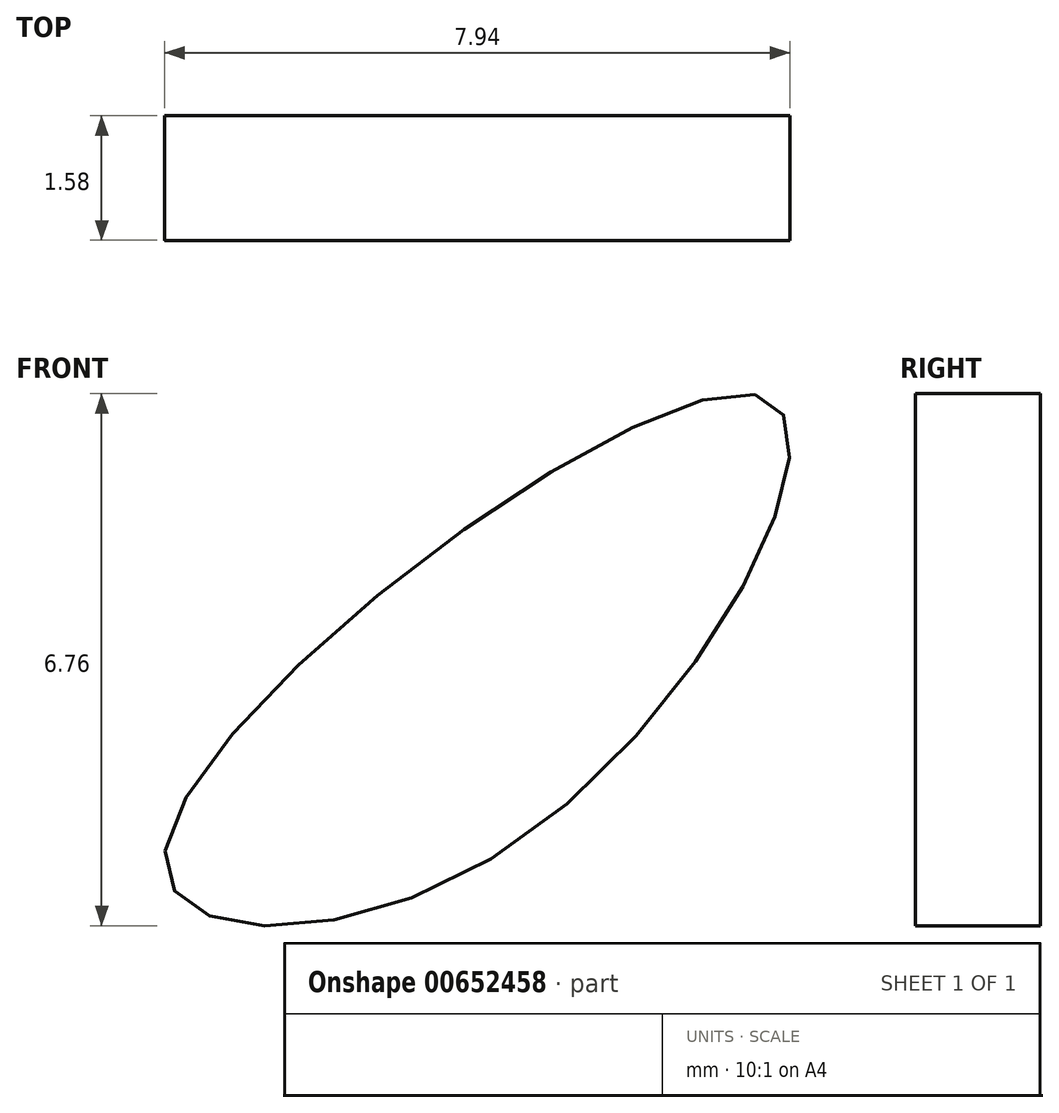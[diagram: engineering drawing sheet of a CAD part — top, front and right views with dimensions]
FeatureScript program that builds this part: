
annotation { "Feature Type Name" : "Feature", "Feature Type Description" : "" }
export const myFeature = defineFeature(function(context is Context, id is Id, definition is map)
    precondition{}
    {
        {
            var Q0;
            Q0=qCreatedBy(makeId("Front.planeOp"),FACE);
            var sketch = newSketch(context, id + "F0", { "sketchPlane" : qUnion([Q0])});
            skFitSpline(sketch, "E0", {"points": [v(-7.57, 0) * mm, v(-3.27, 0) * mm, v(0, 5.78) * mm, v(-7.57, 0) * mm]});
            skSolve(sketch);
        }
        {
            var Q0;
            Q0=makeQuery(id+"F0.imprint","IMPRINT",FACE,{"disambiguationData":[TD([[makeQuery(id+"F0.imprint","IMPRINT",EDGE,{"derivedFrom":sQuery(id+"F0.wireOp",EDGE,"E0")}),1.0]])]});
            extrude(context, id + "F1", {"entities" : qUnion([Q0]), "endBound" : BoundingType.SYMMETRIC, "depth" : 1.59 * mm, "offsetDistance" : 25.4 * mm});
        }
    });
